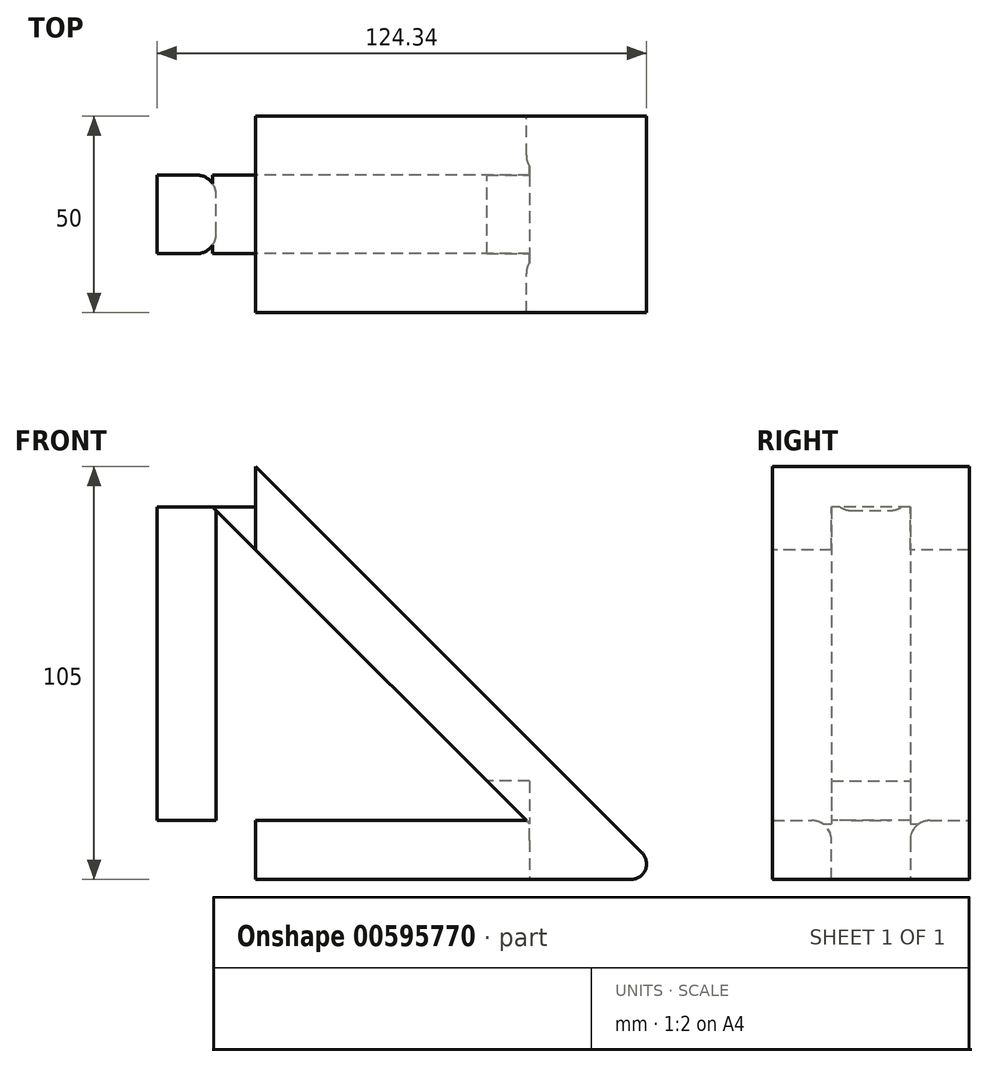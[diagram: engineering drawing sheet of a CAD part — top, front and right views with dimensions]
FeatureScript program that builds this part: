
annotation { "Feature Type Name" : "Feature", "Feature Type Description" : "" }
export const myFeature = defineFeature(function(context is Context, id is Id, definition is map)
    precondition{}
    {
        {
            var Q0;
            Q0=qCreatedBy(makeId("Front.planeOp"),FACE);
            var sketch = newSketch(context, id + "F0", { "sketchPlane" : qUnion([Q0])});
            skLineSegment(sketch, "E0", {"start": v(-102.47, 0) * mm, "end": v(-102.47, 130) * mm});
            skLineSegment(sketch, "E1", {"start": v(-102.47, 130) * mm, "end": v(27.53, 0) * mm});
            skLineSegment(sketch, "E2", {"start": v(27.53, 0) * mm, "end": v(-102.47, 0) * mm});
            skLineSegment(sketch, "E3.0", {"start": v(-87.47, 93.79) * mm, "end": v(-8.68, 15) * mm});
            skLineSegment(sketch, "E3.1", {"start": v(-87.47, 15) * mm, "end": v(-87.47, 93.79) * mm});
            skLineSegment(sketch, "E3.2", {"start": v(-8.68, 15) * mm, "end": v(-87.47, 15) * mm});
            skSolve(sketch);
        }
        {
            var Q0;
            Q0 = qSketchRegion(id + "F0", true);
            extrude(context, id + "F1", {"entities" : qUnion([Q0]), "depth" : 50 * mm, "offsetDistance" : 25 * mm});
        }
        {
            var Q0;
            Q0=makeQuery(id+"F1.opExtrude","SWEPT_FACE",FACE,{"disambiguationData":[OSD([sQuery(id+"F0.wireOp",EDGE,"E1")])]});
            var sketch = newSketch(context, id + "F2", { "sketchPlane" : qUnion([Q0])});
            skLineSegment(sketch, "E4.bottom", {"start": v(-149.38, -15) * mm, "end": v(4.47, -15) * mm});
            skLineSegment(sketch, "E4.top", {"start": v(-149.38, -35) * mm, "end": v(4.47, -35) * mm});
            skLineSegment(sketch, "E4.left", {"start": v(-149.38, -15) * mm, "end": v(-149.38, -35) * mm});
            skLineSegment(sketch, "E4.right", {"start": v(4.47, -15) * mm, "end": v(4.47, -35) * mm});
            skSolve(sketch);
        }
        {
            var Q0;
            Q0=makeQuery(id+"F2.imprint","IMPRINT",FACE,{"disambiguationData":[TD([[makeQuery(id+"F2.imprint","IMPRINT",EDGE,{"derivedFrom":sQuery(id+"F2.wireOp",EDGE,"E4.bottom")}),-1.0]])]});
            extrude(context, id + "F3", {"entities" : qUnion([Q0]), "operationType" : NewBodyOperationType.REMOVE, "oppositeDirection" : true, "depth" : 25 * mm, "offsetDistance" : 25 * mm});
        }
        {
            var Q0;
            Q0=makeQuery(id+"F1.opExtrude","SWEPT_FACE",FACE,{"disambiguationData":[OSD([sQuery(id+"F0.wireOp",EDGE,"E0")])]});
            var sketch = newSketch(context, id + "F4", { "sketchPlane" : qUnion([Q0])});
            skLineSegment(sketch, "E5.bottom", {"start": v(15, 94.64) * mm, "end": v(35, 94.64) * mm});
            skLineSegment(sketch, "E5.top", {"start": v(15, 15) * mm, "end": v(35, 15) * mm});
            skLineSegment(sketch, "E5.left", {"start": v(15, 94.64) * mm, "end": v(15, 15) * mm});
            skLineSegment(sketch, "E5.right", {"start": v(35, 94.64) * mm, "end": v(35, 15) * mm});
            skSolve(sketch);
        }
        {
            var Q0;
            Q0=makeQuery(id+"F4.imprint","IMPRINT",FACE,{"disambiguationData":[TD([[makeQuery(id+"F4.imprint","IMPRINT",EDGE,{"derivedFrom":sQuery(id+"F4.wireOp",EDGE,"E5.bottom")}),1.0]])]});
            extrude(context, id + "F5", {"entities" : qUnion([Q0]), "operationType" : NewBodyOperationType.REMOVE, "oppositeDirection" : true, "depth" : 25 * mm, "offsetDistance" : 25 * mm});
        }
        {
            var Q0;
            Q0=makeQuery(id+"F1.opExtrude","SWEPT_FACE",FACE,{"disambiguationData":[OSD([sQuery(id+"F0.wireOp",EDGE,"E2")])]});
            var sketch = newSketch(context, id + "F6", { "sketchPlane" : qUnion([Q0])});
            skLineSegment(sketch, "E6.bottom", {"start": v(-7.83, 15) * mm, "end": v(-87.47, 15) * mm});
            skLineSegment(sketch, "E6.top", {"start": v(-7.83, 35) * mm, "end": v(-87.47, 35) * mm});
            skLineSegment(sketch, "E6.left", {"start": v(-7.83, 15) * mm, "end": v(-7.83, 35) * mm});
            skLineSegment(sketch, "E6.right", {"start": v(-87.47, 15) * mm, "end": v(-87.47, 35) * mm});
            skSolve(sketch);
        }
        {
            var Q0;
            Q0 = qSketchRegion(id + "F6", true);
            extrude(context, id + "F7", {"entities" : qUnion([Q0]), "operationType" : NewBodyOperationType.REMOVE, "oppositeDirection" : true, "depth" : 25 * mm, "offsetDistance" : 25 * mm});
        }
        {
            var Q0;
            Q0=makeQuery(id+"F1.opExtrude","SWEPT_EDGE",EDGE,{"disambiguationData":[OSD([sQuery(id+"F0.wireOp",EDGE,"E0"),sQuery(id+"F0.wireOp",EDGE,"E2")])]});
            var Q1;
            Q1=makeQuery(id+"F5.boolean.opBoolean","COPY",EDGE,{"derivedFrom":makeQuery(id+"F5.opExtrude","CAP_EDGE",EDGE,{"disambiguationData":[OSD([sQuery(id+"F4.wireOp",EDGE,"E5.top")])],"isStart":true})});
            var Q2;
            Q2=makeQuery(id+"F1.opExtrude","SWEPT_EDGE",EDGE,{"disambiguationData":[OSD([sQuery(id+"F0.wireOp",EDGE,"E0"),sQuery(id+"F0.wireOp",EDGE,"E1")])]});
            var Q3;
            Q3=makeQuery(id+"F3.boolean.opBoolean","INTERSECT",EDGE,{"derivedFrom":[makeQuery(id+"F1.opExtrude","SWEPT_FACE",FACE,{"disambiguationData":[OSD([sQuery(id+"F0.wireOp",EDGE,"E2")])]}),makeQuery(id+"F3.opExtrude","SWEPT_FACE",FACE,{"disambiguationData":[OSD([sQuery(id+"F2.wireOp",EDGE,"E4.right")])]})]});
            var Q4;
            Q4=makeQuery(id+"F3.boolean.opBoolean","INTERSECT",EDGE,{"derivedFrom":[makeQuery(id+"F1.opExtrude","SWEPT_FACE",FACE,{"disambiguationData":[OSD([sQuery(id+"F0.wireOp",EDGE,"E0")])]}),makeQuery(id+"F3.opExtrude","SWEPT_FACE",FACE,{"disambiguationData":[OSD([sQuery(id+"F2.wireOp",EDGE,"E4.left")])]})]});
            var Q5;
            Q5=makeQuery(id+"F1.opExtrude","SWEPT_EDGE",EDGE,{"disambiguationData":[OSD([sQuery(id+"F0.wireOp",EDGE,"E1"),sQuery(id+"F0.wireOp",EDGE,"E2")])]});
            var Q6;
            Q6=makeQuery(id+"F7.boolean.opBoolean","COPY",EDGE,{"derivedFrom":makeQuery(id+"F7.opExtrude","CAP_EDGE",EDGE,{"disambiguationData":[OSD([sQuery(id+"F6.wireOp",EDGE,"E6.right")])],"isStart":true})});
            var Q7;
            Q7=makeQuery(id+"F7.boolean.opBoolean","INTERSECT",EDGE,{"derivedFrom":[makeQuery(id+"F5.boolean.opBoolean","MERGE",FACE,{"derivedFrom":[makeQuery(id+"F1.opExtrude","SWEPT_FACE",FACE,{"disambiguationData":[OSD([sQuery(id+"F0.wireOp",EDGE,"E3.2")])]}),makeQuery(id+"F5.opExtrude","SWEPT_FACE",FACE,{"disambiguationData":[OSD([sQuery(id+"F4.wireOp",EDGE,"E5.top")])]})]}),makeQuery(id+"F7.opExtrude","SWEPT_FACE",FACE,{"disambiguationData":[OSD([sQuery(id+"F6.wireOp",EDGE,"E6.right")])]})]});
            var Q8;
            Q8=makeQuery(id+"F3.boolean.opBoolean","COPY",EDGE,{"derivedFrom":makeQuery(id+"F3.opExtrude","CAP_EDGE",EDGE,{"disambiguationData":[OSD([sQuery(id+"F2.wireOp",EDGE,"E4.right")])],"isStart":true})});
            fillet(context, id + "F8", {"entities" : qUnion([Q0, Q1, Q2, Q3, Q4, Q5, Q6, Q7, Q8]), "radius" : 4 * mm, "tangentPropagation" : true, "allowEdgeOverflow" : false});
        }
        {
            var Q0;
            Q0=makeQuery(id+"F7.boolean.opBoolean","INTERSECT",EDGE,{"derivedFrom":[makeQuery(id+"F5.boolean.opBoolean","MERGE",FACE,{"derivedFrom":[makeQuery(id+"F1.opExtrude","SWEPT_FACE",FACE,{"disambiguationData":[OSD([sQuery(id+"F0.wireOp",EDGE,"E3.2")])]}),makeQuery(id+"F5.opExtrude","SWEPT_FACE",FACE,{"disambiguationData":[OSD([sQuery(id+"F4.wireOp",EDGE,"E5.top")])]})]}),makeQuery(id+"F7.opExtrude","SWEPT_FACE",FACE,{"disambiguationData":[OSD([sQuery(id+"F6.wireOp",EDGE,"E6.top")])]})]});
            var Q1;
            Q1=makeQuery(id+"F7.boolean.opBoolean","INTERSECT",EDGE,{"derivedFrom":[makeQuery(id+"F5.boolean.opBoolean","MERGE",FACE,{"derivedFrom":[makeQuery(id+"F1.opExtrude","SWEPT_FACE",FACE,{"disambiguationData":[OSD([sQuery(id+"F0.wireOp",EDGE,"E3.2")])]}),makeQuery(id+"F5.opExtrude","SWEPT_FACE",FACE,{"disambiguationData":[OSD([sQuery(id+"F4.wireOp",EDGE,"E5.top")])]})]}),makeQuery(id+"F7.opExtrude","SWEPT_FACE",FACE,{"disambiguationData":[OSD([sQuery(id+"F6.wireOp",EDGE,"E6.bottom")])]})]});
            var Q2;
            Q2=makeQuery(id+"F3.boolean.opBoolean","INTERSECT",EDGE,{"derivedFrom":[makeQuery(id+"F1.opExtrude","SWEPT_FACE",FACE,{"disambiguationData":[OSD([sQuery(id+"F0.wireOp",EDGE,"E3.0")])]}),makeQuery(id+"F3.opExtrude","SWEPT_FACE",FACE,{"disambiguationData":[OSD([sQuery(id+"F2.wireOp",EDGE,"E4.bottom")])]})]});
            var Q3;
            Q3=makeQuery(id+"F3.boolean.opBoolean","INTERSECT",EDGE,{"derivedFrom":[makeQuery(id+"F1.opExtrude","SWEPT_FACE",FACE,{"disambiguationData":[OSD([sQuery(id+"F0.wireOp",EDGE,"E3.0")])]}),makeQuery(id+"F3.opExtrude","SWEPT_FACE",FACE,{"disambiguationData":[OSD([sQuery(id+"F2.wireOp",EDGE,"E4.top")])]})]});
            var Q4;
            Q4=makeQuery(id+"F5.boolean.opBoolean","INTERSECT",EDGE,{"derivedFrom":[makeQuery(id+"F1.opExtrude","SWEPT_FACE",FACE,{"disambiguationData":[OSD([sQuery(id+"F0.wireOp",EDGE,"E3.1")])]}),makeQuery(id+"F5.opExtrude","SWEPT_FACE",FACE,{"disambiguationData":[OSD([sQuery(id+"F4.wireOp",EDGE,"E5.left")])]})]});
            var Q5;
            Q5=makeQuery(id+"F5.boolean.opBoolean","INTERSECT",EDGE,{"derivedFrom":[makeQuery(id+"F1.opExtrude","SWEPT_FACE",FACE,{"disambiguationData":[OSD([sQuery(id+"F0.wireOp",EDGE,"E3.1")])]}),makeQuery(id+"F5.opExtrude","SWEPT_FACE",FACE,{"disambiguationData":[OSD([sQuery(id+"F4.wireOp",EDGE,"E5.right")])]})]});
            fillet(context, id + "F9", {"entities" : qUnion([Q0, Q1, Q2, Q3, Q4, Q5]), "radius" : 5 * mm, "tangentPropagation" : true, "allowEdgeOverflow" : false});
        }
    });
